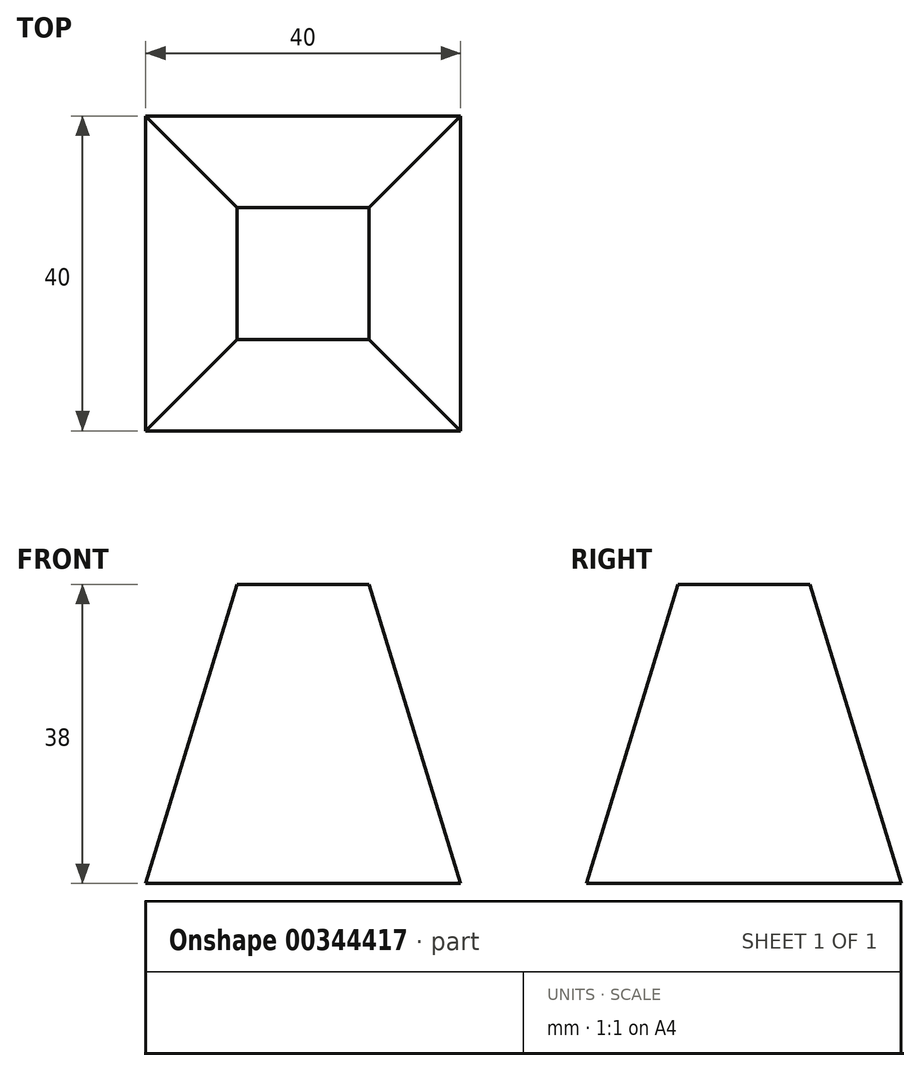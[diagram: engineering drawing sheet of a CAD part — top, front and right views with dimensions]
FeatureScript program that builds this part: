
annotation { "Feature Type Name" : "Feature", "Feature Type Description" : "" }
export const myFeature = defineFeature(function(context is Context, id is Id, definition is map)
    precondition{}
    {
        {
            var Q0;
            Q0=qCreatedBy(makeId("Top.planeOp"),FACE);
            var sketch = newSketch(context, id + "F0", { "sketchPlane" : qUnion([Q0])});
            skLineSegment(sketch, "E0.bottom", {"start": v(0, 0) * mm, "end": v(40, 0) * mm});
            skLineSegment(sketch, "E0.top", {"start": v(0, -40) * mm, "end": v(40, -40) * mm});
            skLineSegment(sketch, "E0.left", {"start": v(0, 0) * mm, "end": v(0, -40) * mm});
            skLineSegment(sketch, "E0.right", {"start": v(40, 0) * mm, "end": v(40, -40) * mm});
            skSolve(sketch);
        }
        {
            var Q0;
            Q0=makeQuery(id+"F0.imprint","IMPRINT",FACE,{"disambiguationData":[TD([[makeQuery(id+"F0.imprint","IMPRINT",EDGE,{"derivedFrom":sQuery(id+"F0.wireOp",EDGE,"E0.bottom")}),-1.0]])]});
            extrude(context, id + "F1", {"entities" : qUnion([Q0]), "depth" : 38 * mm, "hasDraft" : true, "draftAngle" : 17 * degree, "draftPullDirection" : true});
        }
    });
